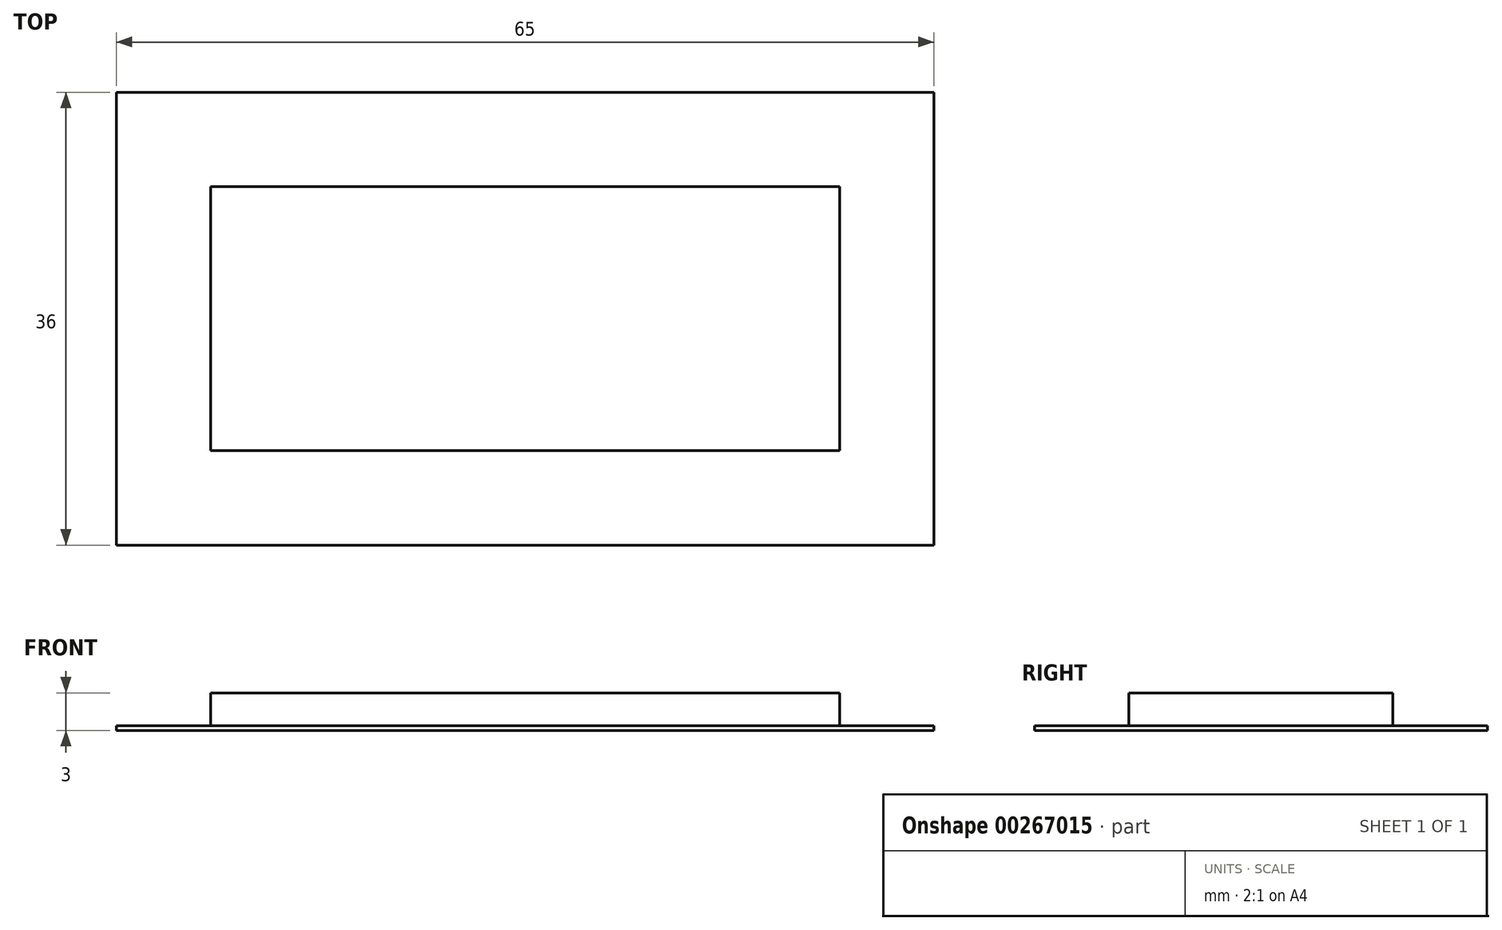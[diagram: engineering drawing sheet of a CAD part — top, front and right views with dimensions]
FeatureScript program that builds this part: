
annotation { "Feature Type Name" : "Feature", "Feature Type Description" : "" }
export const myFeature = defineFeature(function(context is Context, id is Id, definition is map)
    precondition{}
    {
        {
            var Q0;
            Q0=qCreatedBy(makeId("Top.planeOp"),FACE);
            var sketch = newSketch(context, id + "F0", { "sketchPlane" : qUnion([Q0])});
            skLineSegment(sketch, "E0.bottom", {"start": v(32.5, -18) * mm, "end": v(-32.5, -18) * mm});
            skLineSegment(sketch, "E0.top", {"start": v(32.5, 18) * mm, "end": v(-32.5, 18) * mm});
            skLineSegment(sketch, "E0.left", {"start": v(32.5, -18) * mm, "end": v(32.5, 18) * mm});
            skLineSegment(sketch, "E0.right", {"start": v(-32.5, -18) * mm, "end": v(-32.5, 18) * mm});
            skPoint(sketch, "E0.middle", {"position": v(0, 0) * mm});
            skLineSegment(sketch, "E1.bottom", {"start": v(25, -10.5) * mm, "end": v(-25, -10.5) * mm});
            skLineSegment(sketch, "E1.top", {"start": v(25, 10.5) * mm, "end": v(-25, 10.5) * mm});
            skLineSegment(sketch, "E1.left", {"start": v(25, -10.5) * mm, "end": v(25, 10.5) * mm});
            skLineSegment(sketch, "E1.right", {"start": v(-25, -10.5) * mm, "end": v(-25, 10.5) * mm});
            skSolve(sketch);
        }
        {
            var Q0;
            Q0=makeQuery(id+"F0.imprint","IMPRINT",FACE,{"disambiguationData":[TD([[makeQuery(id+"F0.imprint","IMPRINT",EDGE,{"derivedFrom":sQuery(id+"F0.wireOp",EDGE,"E0.bottom")}),-1.0]])]});
            var Q1;
            Q1=makeQuery(id+"F0.imprint","IMPRINT",FACE,{"disambiguationData":[TD([[makeQuery(id+"F0.imprint","IMPRINT",EDGE,{"derivedFrom":sQuery(id+"F0.wireOp",EDGE,"E1.bottom")}),-1.0]])]});
            extrude(context, id + "F1", {"entities" : qUnion([Q0, Q1]), "depth" : .4 * mm});
        }
        {
            var Q0;
            Q0=makeQuery(id+"F0.imprint","IMPRINT",FACE,{"disambiguationData":[TD([[makeQuery(id+"F0.imprint","IMPRINT",EDGE,{"derivedFrom":sQuery(id+"F0.wireOp",EDGE,"E1.bottom")}),-1.0]])]});
            extrude(context, id + "F2", {"entities" : qUnion([Q0]), "operationType" : NewBodyOperationType.ADD, "depth" : 3 * mm});
        }
    });
